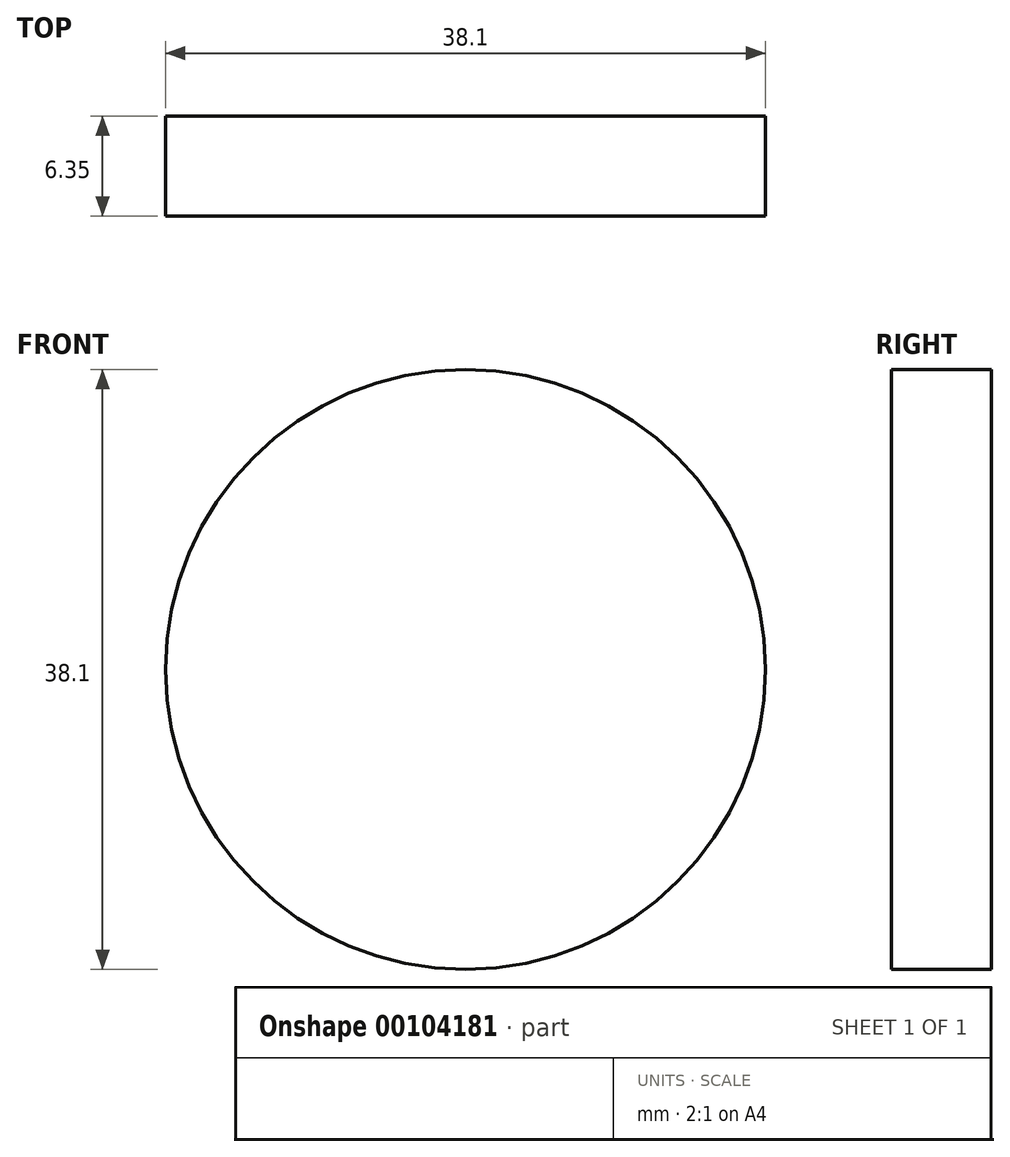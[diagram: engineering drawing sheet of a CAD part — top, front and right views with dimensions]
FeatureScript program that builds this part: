
annotation { "Feature Type Name" : "Feature", "Feature Type Description" : "" }
export const myFeature = defineFeature(function(context is Context, id is Id, definition is map)
    precondition{}
    {
        {
            var Q0;
            Q0=qCreatedBy(makeId("Front.planeOp"),FACE);
            var sketch = newSketch(context, id + "F0", { "sketchPlane" : qUnion([Q0])});
            skCircle(sketch, "E0", {"center": v(-28.94, 24.28) * mm, "radius": 19.05 * mm});
            skSolve(sketch);
        }
        {
            var Q0;
            Q0 = qSketchRegion(id + "F0", true);
            extrude(context, id + "F1", {"entities" : qUnion([Q0]), "depth" : 6.35 * mm});
        }
    });
